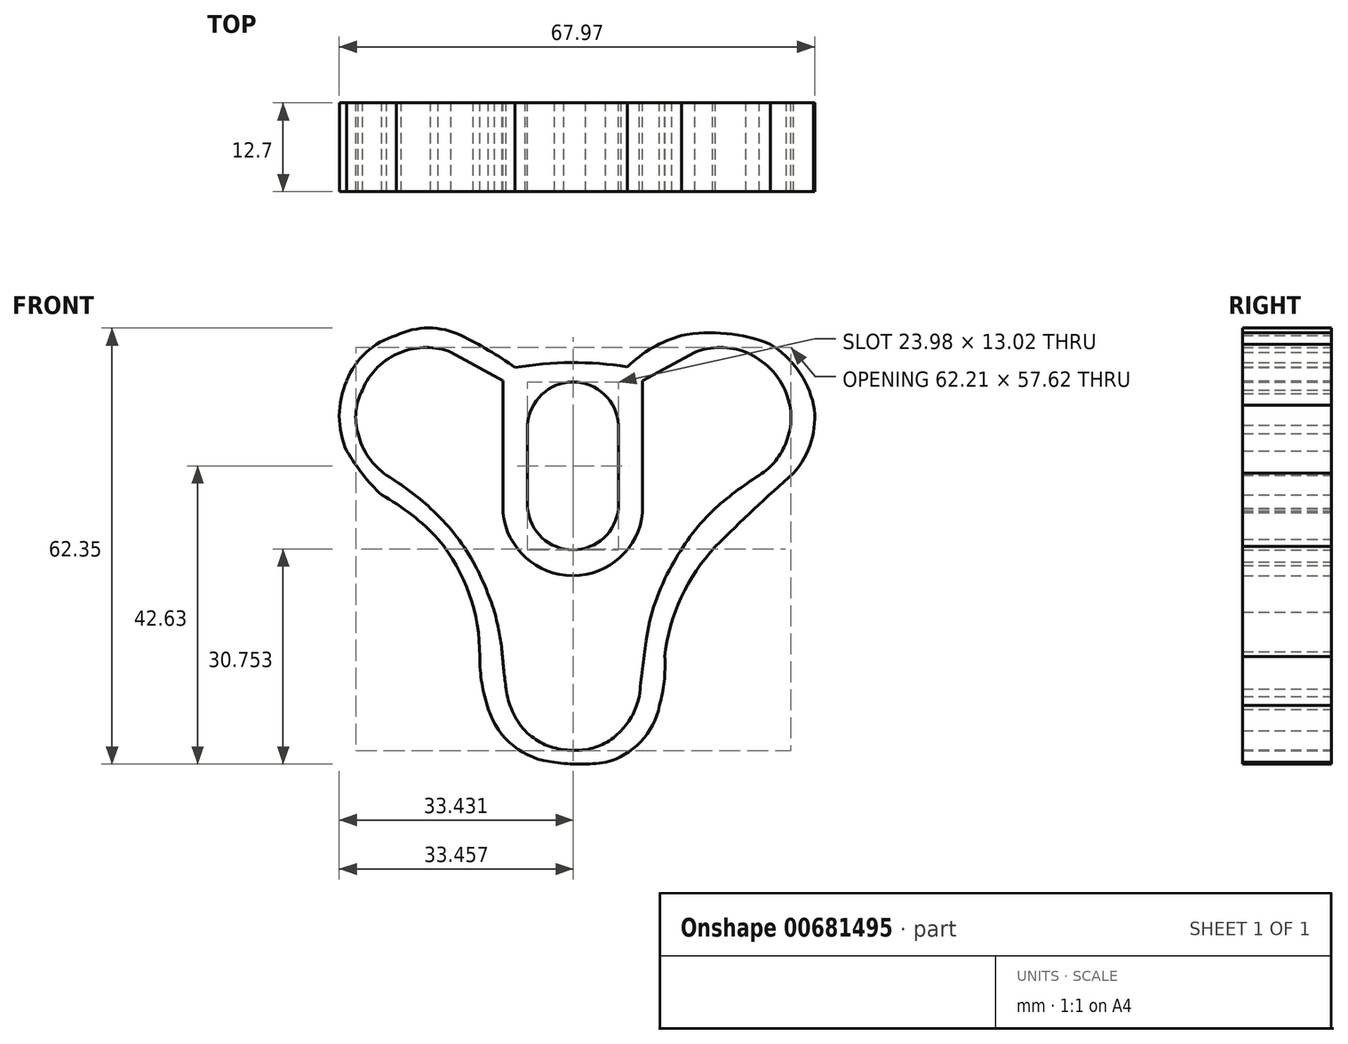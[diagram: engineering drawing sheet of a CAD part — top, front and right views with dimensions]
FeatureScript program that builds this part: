
annotation { "Feature Type Name" : "Feature", "Feature Type Description" : "" }
export const myFeature = defineFeature(function(context is Context, id is Id, definition is map)
    precondition{}
    {
        {
            var Q0;
            Q0=qCreatedBy(makeId("Front.planeOp"),FACE);
            var sketch = newSketch(context, id + "F0", { "sketchPlane" : qUnion([Q0])});
            skLineSegment(sketch, "E0", {"start": v(-6.57, 12.5) * mm, "end": v(-6.57, 0.62) * mm});
            skArc(sketch, "E1", {"start": v(6.45, 12.5) * mm, "mid": v(-0.06, 18.64) * mm, "end": v(-6.57, 12.5) * mm});
            skArc(sketch, "E2", {"start": v(-6.57, 0.62) * mm, "mid": v(-0.08, -5.34) * mm, "end": v(6.42, 0.62) * mm});
            skLineSegment(sketch, "E3", {"start": v(6.45, 12.5) * mm, "end": v(6.42, 0.62) * mm});
            skLineSegment(sketch, "E4", {"start": v(9.88, 18.8) * mm, "end": v(9.88, 0) * mm});
            skLineSegment(sketch, "E5", {"start": v(-10.08, 18.8) * mm, "end": v(-10.08, 0) * mm});
            skArc(sketch, "E6", {"start": v(-10.08, 0) * mm, "mid": v(-0.1, -9.06) * mm, "end": v(9.88, 0) * mm});
            skLineSegment(sketch, "E7", {"start": v(-10.08, 18.8) * mm, "end": v(-17.5, 22.9) * mm});
            skLineSegment(sketch, "E8", {"start": v(9.88, 18.8) * mm, "end": v(17.33, 22.9) * mm});
            skArc(sketch, "E9", {"start": v(24.65, 22.9) * mm, "mid": v(21, 23.58) * mm, "end": v(17.33, 22.9) * mm});
            skArc(sketch, "E10", {"start": v(30.43, 17.02) * mm, "mid": v(28.13, 20.54) * mm, "end": v(24.65, 22.9) * mm});
            skArc(sketch, "E11", {"start": v(30.43, 10.1) * mm, "mid": v(31.07, 13.56) * mm, "end": v(30.43, 17.02) * mm});
            skArc(sketch, "E12", {"start": v(26.57, 5.31) * mm, "mid": v(28.88, 7.4) * mm, "end": v(30.43, 10.1) * mm});
            skArc(sketch, "E13", {"start": v(26.57, 5.31) * mm, "mid": v(23.1, 2.93) * mm, "end": v(19.88, 0.23) * mm});
            skArc(sketch, "E14", {"start": v(19.88, 0.23) * mm, "mid": v(16.66, -3.46) * mm, "end": v(14.07, -7.61) * mm});
            skArc(sketch, "E15", {"start": v(14.07, -7.61) * mm, "mid": v(11.69, -12.83) * mm, "end": v(10.38, -18.4) * mm});
            skArc(sketch, "E16", {"start": v(10.38, -18.4) * mm, "mid": v(9.88, -22.38) * mm, "end": v(9.38, -26.34) * mm});
            skArc(sketch, "E17", {"start": v(-17.5, 22.9) * mm, "mid": v(-21.07, 23.57) * mm, "end": v(-24.64, 22.9) * mm});
            skArc(sketch, "E18", {"start": v(-24.64, 22.9) * mm, "mid": v(-27.97, 20.79) * mm, "end": v(-30.17, 17.52) * mm});
            skArc(sketch, "E19", {"start": v(-30.17, 17.52) * mm, "mid": v(-31.1, 14.45) * mm, "end": v(-30.8, 11.25) * mm});
            skArc(sketch, "E20", {"start": v(-30.8, 11.25) * mm, "mid": v(-29.3, 7.9) * mm, "end": v(-26.7, 5.31) * mm});
            skArc(sketch, "E21", {"start": v(-20.42, 0.57) * mm, "mid": v(-23.46, 3.08) * mm, "end": v(-26.7, 5.31) * mm});
            skArc(sketch, "E22", {"start": v(-14.34, -7.07) * mm, "mid": v(-17.08, -3) * mm, "end": v(-20.42, 0.57) * mm});
            skArc(sketch, "E23", {"start": v(-11.28, -14.26) * mm, "mid": v(-12.65, -10.6) * mm, "end": v(-14.34, -7.07) * mm});
            skArc(sketch, "E24", {"start": v(-10.2, -19.92) * mm, "mid": v(-10.66, -17.07) * mm, "end": v(-11.28, -14.26) * mm});
            skArc(sketch, "E25", {"start": v(-10.2, -19.92) * mm, "mid": v(-9.96, -22.59) * mm, "end": v(-9.63, -25.24) * mm});
            skArc(sketch, "E26", {"start": v(-9.63, -25.24) * mm, "mid": v(-8.75, -28.44) * mm, "end": v(-6.92, -31.22) * mm});
            skArc(sketch, "E27", {"start": v(6.78, -31.22) * mm, "mid": v(8.43, -28.97) * mm, "end": v(9.38, -26.34) * mm});
            skArc(sketch, "E28", {"start": v(1.72, -33.9) * mm, "mid": v(4.49, -33) * mm, "end": v(6.78, -31.22) * mm});
            skArc(sketch, "E29", {"start": v(-6.92, -31.22) * mm, "mid": v(-4.38, -33.05) * mm, "end": v(-1.38, -33.9) * mm});
            skArc(sketch, "E30", {"start": v(-1.38, -33.9) * mm, "mid": v(0.17, -34.03) * mm, "end": v(1.72, -33.9) * mm});
            skArc(sketch, "E31", {"start": v(-8.35, 20.72) * mm, "mid": v(-12.12, 23.18) * mm, "end": v(-16.08, 25.3) * mm});
            skArc(sketch, "E32", {"start": v(-16.08, 25.3) * mm, "mid": v(-20.71, 26.37) * mm, "end": v(-25.34, 25.3) * mm});
            skArc(sketch, "E33", {"start": v(-25.34, 25.3) * mm, "mid": v(-29.65, 22.9) * mm, "end": v(-32.4, 18.8) * mm});
            skArc(sketch, "E34", {"start": v(-32.4, 18.8) * mm, "mid": v(-33.49, 13.79) * mm, "end": v(-32.4, 8.78) * mm});
            skArc(sketch, "E35", {"start": v(-32.4, 8.78) * mm, "mid": v(-30.14, 5.47) * mm, "end": v(-27.44, 2.48) * mm});
            skArc(sketch, "E36", {"start": v(-19.33, -3.82) * mm, "mid": v(-23.12, -0.33) * mm, "end": v(-27.44, 2.48) * mm});
            skArc(sketch, "E37", {"start": v(-13.4, -20.63) * mm, "mid": v(-14.89, -11.7) * mm, "end": v(-19.33, -3.82) * mm});
            skArc(sketch, "E38", {"start": v(-13.4, -20.63) * mm, "mid": v(-13.1, -24.45) * mm, "end": v(-12.15, -28.17) * mm});
            skArc(sketch, "E39", {"start": v(-12.15, -28.17) * mm, "mid": v(-8.6, -33.4) * mm, "end": v(-2.72, -35.71) * mm});
            skArc(sketch, "E40", {"start": v(-2.72, -35.71) * mm, "mid": v(0.94, -35.98) * mm, "end": v(4.59, -35.71) * mm});
            skArc(sketch, "E41", {"start": v(31.46, 5.63) * mm, "mid": v(34, 10.18) * mm, "end": v(34.33, 15.37) * mm});
            skArc(sketch, "E42", {"start": v(15.42, 25.3) * mm, "mid": v(11.28, 23.53) * mm, "end": v(7.7, 20.81) * mm});
            skArc(sketch, "E43", {"start": v(7.7, 20.81) * mm, "mid": v(-0.33, 21.42) * mm, "end": v(-8.35, 20.72) * mm});
            skArc(sketch, "E44", {"start": v(4.59, -35.71) * mm, "mid": v(9.63, -32.79) * mm, "end": v(12.27, -27.6) * mm});
            skArc(sketch, "E45", {"start": v(12.27, -27.6) * mm, "mid": v(12.95, -24.14) * mm, "end": v(13.04, -20.63) * mm});
            skArc(sketch, "E46", {"start": v(20.3, -4.87) * mm, "mid": v(15.39, -12.16) * mm, "end": v(13.04, -20.63) * mm});
            skArc(sketch, "E47", {"start": v(31.46, 5.63) * mm, "mid": v(25.8, 0.46) * mm, "end": v(20.3, -4.87) * mm});
            skArc(sketch, "E48", {"start": v(34.33, 15.37) * mm, "mid": v(32.09, 20.33) * mm, "end": v(28.12, 24.06) * mm});
            skArc(sketch, "E49", {"start": v(28.12, 24.06) * mm, "mid": v(21.86, 25.58) * mm, "end": v(15.42, 25.3) * mm});
            skSolve(sketch);
        }
        {
            var Q0;
            Q0=makeQuery(id+"F0.imprint","IMPRINT",FACE,{"disambiguationData":[TD([[makeQuery(id+"F0.imprint","IMPRINT",EDGE,{"derivedFrom":sQuery(id+"F0.wireOp",EDGE,"E0")}),-1.0]])]});
            extrude(context, id + "F1", {"entities" : qUnion([Q0]), "depth" : 12.7 * mm, "offsetDistance" : 25.4 * mm});
        }
    });
